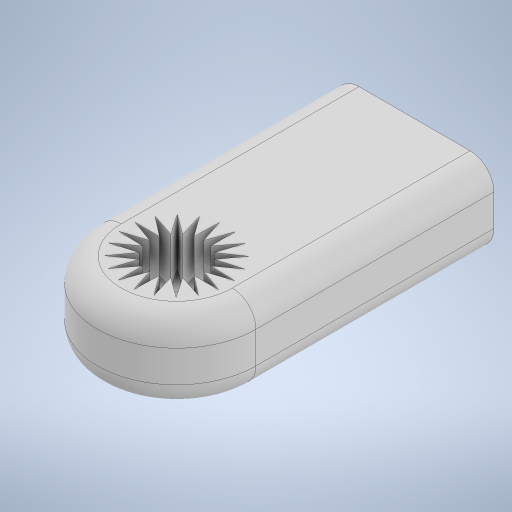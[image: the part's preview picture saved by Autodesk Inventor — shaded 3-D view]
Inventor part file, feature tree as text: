
AUTODESK INVENTOR PART (.ipt)
format: ipt  version: 2023.1 (Build 271208000, 208)  size: 377,344 bytes
history: native  units: mm
features: other x4, extrude x2, plane x1, fillet x1, projected_geometry x1
ambient origin geometry x8: Origin, YZ Plane, XZ Plane, XY Plane, X Axis, Y Axis, Z Axis, Center Point
bodies: Solid1 (feature_tree)
feature tree (9):
  extrude  "Horn Base"  Depth=10.0mm
  extrude  "Servo Spline Cut"  Depth=20.0mm
  plane  "Work Plane (Clip Axis)"
  other  "Fin Clip Cut"
  fillet  "Fillets (Horn Edges)"  Radius=3.0mm
  other  "Horn Base Profile"
  other  "Spline Profile"
  other  "Clip Cut Profile"
  projected_geometry  "Projected Loop1"
